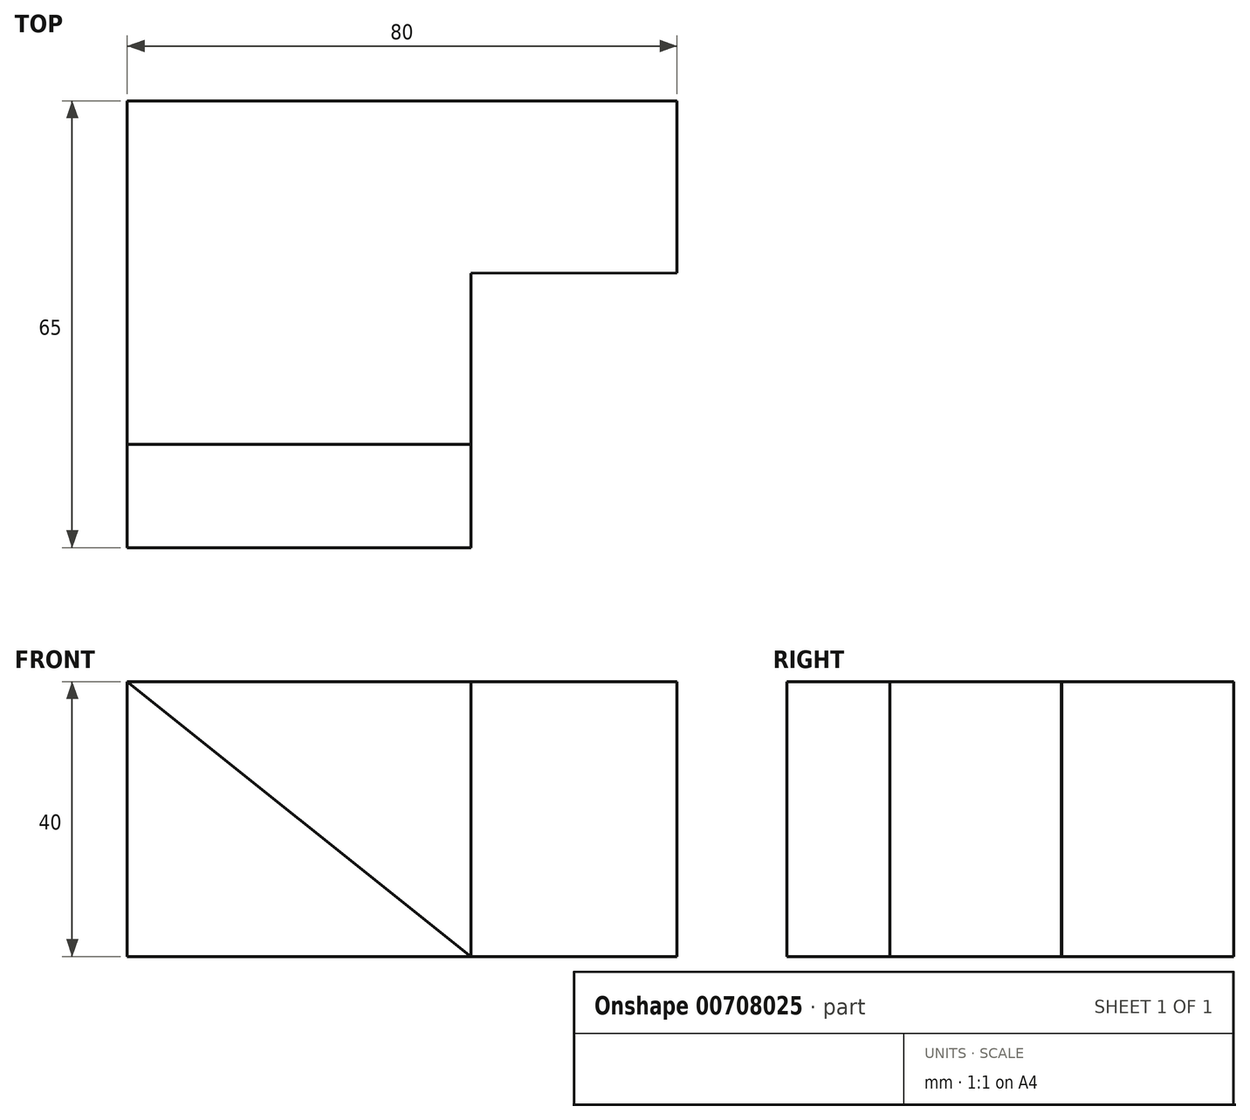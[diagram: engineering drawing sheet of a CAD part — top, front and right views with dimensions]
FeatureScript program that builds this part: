
annotation { "Feature Type Name" : "Feature", "Feature Type Description" : "" }
export const myFeature = defineFeature(function(context is Context, id is Id, definition is map)
    precondition{}
    {
        {
            var Q0;
            Q0=qCreatedBy(makeId("Front.planeOp"),FACE);
            var sketch = newSketch(context, id + "F0", { "sketchPlane" : qUnion([Q0])});
            skLineSegment(sketch, "E0", {"start": v(0, 0) * mm, "end": v(0, 40) * mm});
            skLineSegment(sketch, "E1", {"start": v(0, 0) * mm, "end": v(50, 0) * mm});
            skLineSegment(sketch, "E2", {"start": v(50, 0) * mm, "end": v(0, 40) * mm});
            skSolve(sketch);
        }
        {
            var Q0;
            Q0=makeQuery(id+"F0.imprint","IMPRINT",FACE,{"disambiguationData":[TD([[makeQuery(id+"F0.imprint","IMPRINT",EDGE,{"derivedFrom":sQuery(id+"F0.wireOp",EDGE,"E0")}),-1.0]])]});
            extrude(context, id + "F1", {"entities" : qUnion([Q0]), "depth" : 15 * mm, "offsetDistance" : 25 * mm});
        }
        {
            var Q0;
            Q0=qCreatedBy(makeId("Top.planeOp"),FACE);
            var sketch = newSketch(context, id + "F2", { "sketchPlane" : qUnion([Q0])});
            skLineSegment(sketch, "E3", {"start": v(0, 0) * mm, "end": v(0, 50) * mm});
            skLineSegment(sketch, "E4", {"start": v(0, 50) * mm, "end": v(80, 50) * mm});
            skLineSegment(sketch, "E5", {"start": v(80, 50) * mm, "end": v(80, 25) * mm});
            skLineSegment(sketch, "E6", {"start": v(0, 0) * mm, "end": v(50, 0) * mm});
            skLineSegment(sketch, "E7", {"start": v(50, 0) * mm, "end": v(50, 24.92) * mm});
            skLineSegment(sketch, "E8", {"start": v(50, 24.92) * mm, "end": v(80, 25) * mm});
            skSolve(sketch);
        }
        {
            var Q0;
            Q0=makeQuery(id+"F2.imprint","IMPRINT",FACE,{"disambiguationData":[TD([[makeQuery(id+"F2.imprint","IMPRINT",EDGE,{"derivedFrom":sQuery(id+"F2.wireOp",EDGE,"E3")}),-1.0]])]});
            extrude(context, id + "F3", {"entities" : qUnion([Q0]), "operationType" : NewBodyOperationType.ADD, "depth" : 40 * mm, "offsetDistance" : 25 * mm});
        }
    });
